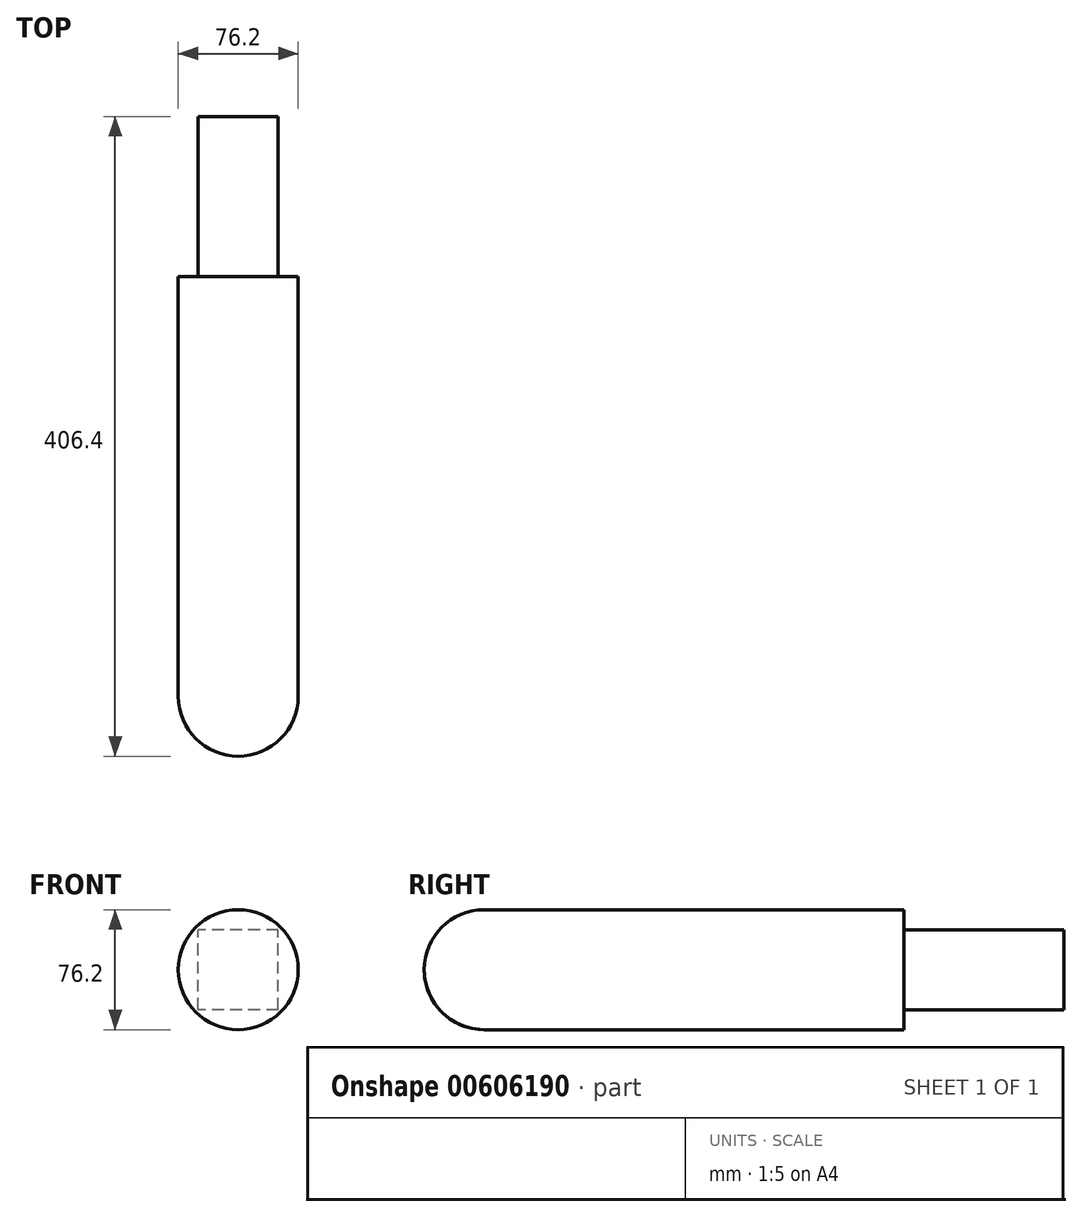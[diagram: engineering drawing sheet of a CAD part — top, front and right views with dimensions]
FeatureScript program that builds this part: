
annotation { "Feature Type Name" : "Feature", "Feature Type Description" : "" }
export const myFeature = defineFeature(function(context is Context, id is Id, definition is map)
    precondition{}
    {
        {
            var Q0;
            Q0=qCreatedBy(makeId("Front.planeOp"),FACE);
            var sketch = newSketch(context, id + "F0", { "sketchPlane" : qUnion([Q0])});
            skLineSegment(sketch, "E0.bottom", {"start": v(25.4, -25.4) * mm, "end": v(-25.4, -25.4) * mm});
            skLineSegment(sketch, "E0.top", {"start": v(25.4, 25.4) * mm, "end": v(-25.4, 25.4) * mm});
            skLineSegment(sketch, "E0.left", {"start": v(25.4, -25.4) * mm, "end": v(25.4, 25.4) * mm});
            skLineSegment(sketch, "E0.right", {"start": v(-25.4, -25.4) * mm, "end": v(-25.4, 25.4) * mm});
            skPoint(sketch, "E0.middle", {"position": v(0, 0) * mm});
            skSolve(sketch);
        }
        {
            var Q0;
            Q0 = qSketchRegion(id + "F0", true);
            extrude(context, id + "F1", {"entities" : qUnion([Q0]), "depth" : 101.6 * mm, "offsetDistance" : 25.4 * mm});
        }
        {
            var Q0;
            Q0=makeQuery(id+"F1.opExtrude","CAP_FACE",FACE,{"disambiguationData":[OSD([sQuery(id+"F0.wireOp",EDGE,"E0.bottom"),sQuery(id+"F0.wireOp",EDGE,"E0.top"),sQuery(id+"F0.wireOp",EDGE,"E0.left"),sQuery(id+"F0.wireOp",EDGE,"E0.right")])],"isStart":false});
            var sketch = newSketch(context, id + "F2", { "sketchPlane" : qUnion([Q0])});
            skCircle(sketch, "E1", {"center": v(0, 0) * mm, "radius": 38.1 * mm});
            skSolve(sketch);
        }
        {
            var Q0;
            Q0 = qSketchRegion(id + "F2", true);
            extrude(context, id + "F3", {"entities" : qUnion([Q0]), "operationType" : NewBodyOperationType.ADD, "depth" : 304.8 * mm, "offsetDistance" : 25.4 * mm});
        }
        {
            var Q0;
            Q0=makeQuery(id+"F3.opExtrude","CAP_EDGE",EDGE,{"disambiguationData":[OSD([sQuery(id+"F2.wireOp",EDGE,"E1")])],"isStart":false});
            fillet(context, id + "F4", {"entities" : qUnion([Q0]), "radius" : 38.1 * mm, "tangentPropagation" : true, "allowEdgeOverflow" : false});
        }
    });
